# Revit family: VTi.931.I_Фитинг_пресс-тройник_Нерж_VALTEC
name_source: partatom
category: Соединительные детали трубопроводов
units: mm (PartAtom-declared; Revit-internal decimal feet)

## family parameters
Всегда вертикально = Да
На основе рабочей плоскости = Нет
Общий = Нет
При загрузке вырезать с полостями = Нет
Размер круглого соединителя = Использовать диаметр
Тип детали = Тройник

## types (21) — shared parameters
ADSK_Единица измерения = шт.
ADSK_Количество = 1
ADSK_Материал = Сталь, нержавеющая - VALTEC
LT = VTi.931.I_Фитинг_пресс-тройник_Нерж_VALTEC
zero-valued in all types: Отметка по умолчанию

## type names (no varying parameters)
- Фитинг из нержавеющей стали -  пресс-тройник 15х12х15 мм
- Фитинг из нержавеющей стали -  пресс-тройник 15х15х15 мм
- Фитинг из нержавеющей стали -  пресс-тройник 18х15х18 мм
- Фитинг из нержавеющей стали -  пресс-тройник 18х18х18 мм
- Фитинг из нержавеющей стали -  пресс-тройник 22х15х22 мм
- Фитинг из нержавеющей стали -  пресс-тройник 22х18х22 мм
- Фитинг из нержавеющей стали -  пресс-тройник 22х22х22 мм
- Фитинг из нержавеющей стали -  пресс-тройник 28х15х28 мм
- Фитинг из нержавеющей стали -  пресс-тройник 28х22х22 мм
- Фитинг из нержавеющей стали -  пресс-тройник 28х28х22 мм
- Фитинг из нержавеющей стали -  пресс-тройник 28х22х28 мм
- Фитинг из нержавеющей стали -  пресс-тройник 28х28х28 мм
- Фитинг из нержавеющей стали -  пресс-тройник 35х22х35 мм
- Фитинг из нержавеющей стали -  пресс-тройник 35х35х35 мм
- Фитинг из нержавеющей стали -  пресс-тройник 35х15х35 мм
- Фитинг из нержавеющей стали -  пресс-тройник 35х28х35 мм
- Фитинг из нержавеющей стали -  пресс-тройник 42х35х42 мм
- Фитинг из нержавеющей стали -  пресс-тройник 42х42х42 мм
- Фитинг из нержавеющей стали -  пресс-тройник 54х42х54 мм
- Фитинг из нержавеющей стали -  пресс-тройник 54х54х54 мм
- Фитинг из нержавеющей стали -  пресс-тройник 76х54х76 мм
